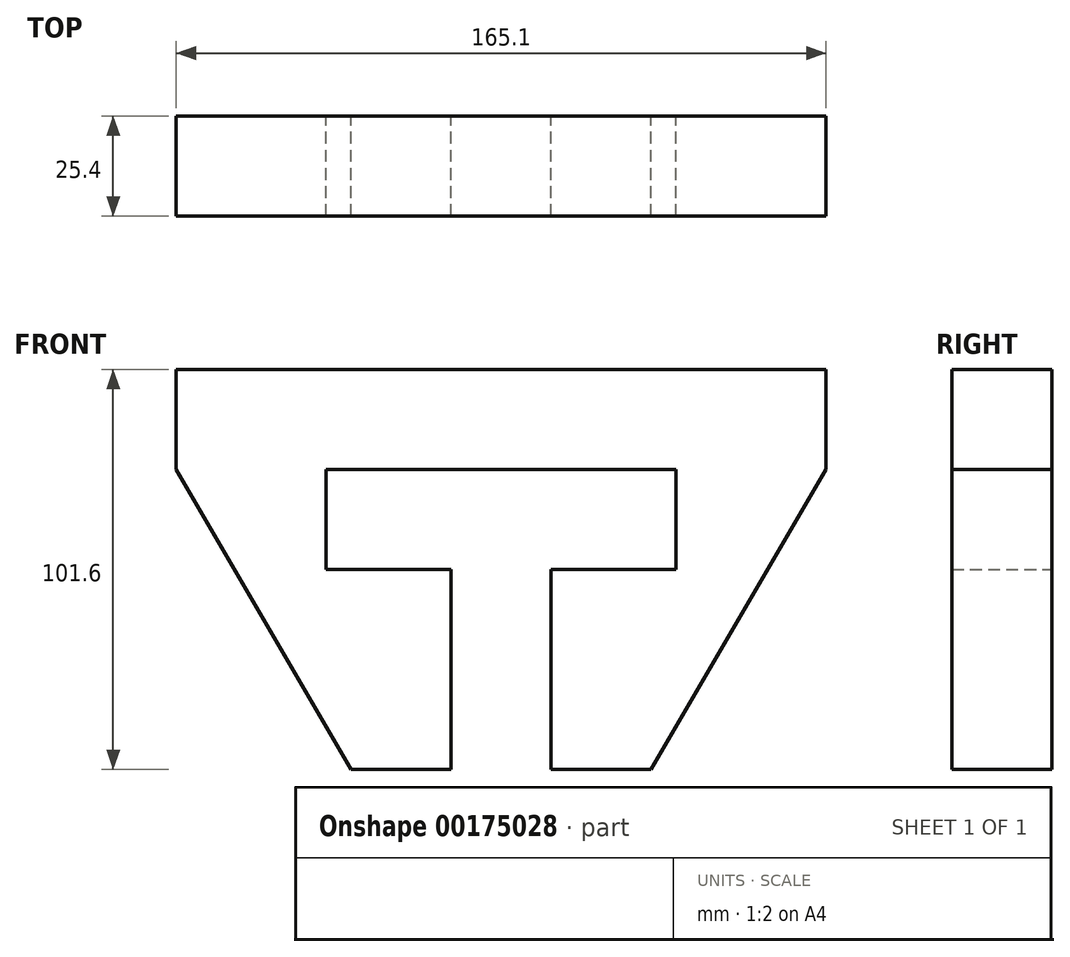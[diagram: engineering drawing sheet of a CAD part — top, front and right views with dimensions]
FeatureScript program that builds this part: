
annotation { "Feature Type Name" : "Feature", "Feature Type Description" : "" }
export const myFeature = defineFeature(function(context is Context, id is Id, definition is map)
    precondition{}
    {
        {
            var Q0;
            Q0=qCreatedBy(makeId("Front.planeOp"),FACE);
            var sketch = newSketch(context, id + "F0", { "sketchPlane" : qUnion([Q0])});
            skLineSegment(sketch, "E0", {"start": v(-104.95, 0) * mm, "end": v(-60.5, -76.2) * mm});
            skLineSegment(sketch, "E1", {"start": v(-104.95, 0) * mm, "end": v(-104.95, 25.4) * mm});
            skLineSegment(sketch, "E2", {"start": v(-104.95, 25.4) * mm, "end": v(60.15, 25.4) * mm});
            skLineSegment(sketch, "E3", {"start": v(60.15, 25.4) * mm, "end": v(60.15, 0) * mm});
            skLineSegment(sketch, "E4", {"start": v(60.15, 0) * mm, "end": v(15.7, -76.2) * mm});
            skLineSegment(sketch, "E5", {"start": v(-60.5, -76.2) * mm, "end": v(-35.1, -76.2) * mm});
            skLineSegment(sketch, "E6", {"start": v(15.7, -76.2) * mm, "end": v(-9.7, -76.2) * mm});
            skLineSegment(sketch, "E7", {"start": v(-35.1, -76.2) * mm, "end": v(-35.1, -25.4) * mm});
            skLineSegment(sketch, "E8", {"start": v(-9.7, -76.2) * mm, "end": v(-9.7, -25.4) * mm});
            skLineSegment(sketch, "E9", {"start": v(-35.1, -25.4) * mm, "end": v(-66.85, -25.4) * mm});
            skLineSegment(sketch, "E10", {"start": v(-9.7, -25.4) * mm, "end": v(22.05, -25.4) * mm});
            skLineSegment(sketch, "E11", {"start": v(-66.85, -25.4) * mm, "end": v(-66.85, 0) * mm});
            skLineSegment(sketch, "E12", {"start": v(22.05, -25.4) * mm, "end": v(22.05, 0) * mm});
            skLineSegment(sketch, "E13", {"start": v(-66.85, 0) * mm, "end": v(22.05, 0) * mm});
            skSolve(sketch);
        }
        {
            var Q0;
            Q0 = qSketchRegion(id + "F0", true);
            extrude(context, id + "F1", {"entities" : qUnion([Q0]), "depth" : 25.4 * mm});
        }
    });
